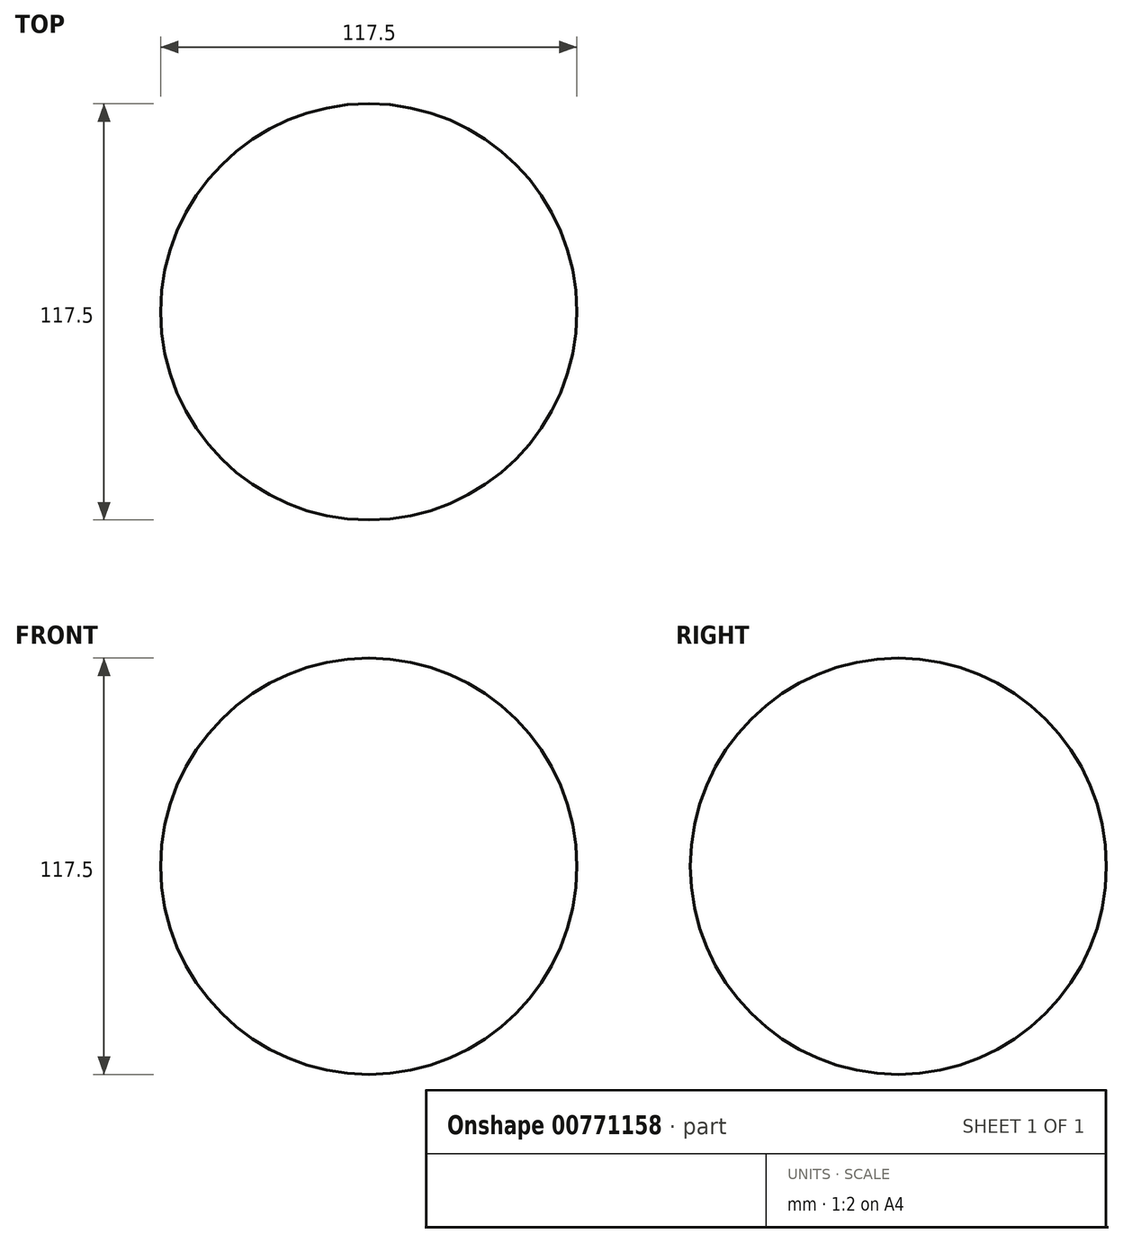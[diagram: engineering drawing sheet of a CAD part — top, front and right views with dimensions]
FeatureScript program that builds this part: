
annotation { "Feature Type Name" : "Feature", "Feature Type Description" : "" }
export const myFeature = defineFeature(function(context is Context, id is Id, definition is map)
    precondition{}
    {
        {
            var Q0;
            Q0=qCreatedBy(makeId("Front.planeOp"),FACE);
            var sketch = newSketch(context, id + "F0", { "sketchPlane" : qUnion([Q0])});
            skArc(sketch, "E0", {"start": v(0, 58.75) * mm, "mid": v(-58.75, 0) * mm, "end": v(0, -58.75) * mm});
            skLineSegment(sketch, "E1", {"start": v(0, 58.75) * mm, "end": v(0, -58.75) * mm});
            skSolve(sketch);
        }
        {
            var Q0;
            Q0=makeQuery(id+"F0.imprint","IMPRINT",FACE,{"disambiguationData":[TD([[makeQuery(id+"F0.imprint","IMPRINT",EDGE,{"derivedFrom":sQuery(id+"F0.wireOp",EDGE,"E0")}),1.0]])]});
            var Q1;
            Q1=sQuery(id+"F0.wireOp",EDGE,"E1");
            revolve(context, id + "F1", {"surfaceOperationType" : NewSurfaceOperationType.NEW, "entities" : qUnion([Q0]), "axis" : qUnion([Q1]), "revolveType" : RevolveType.FULL});
        }
    });
